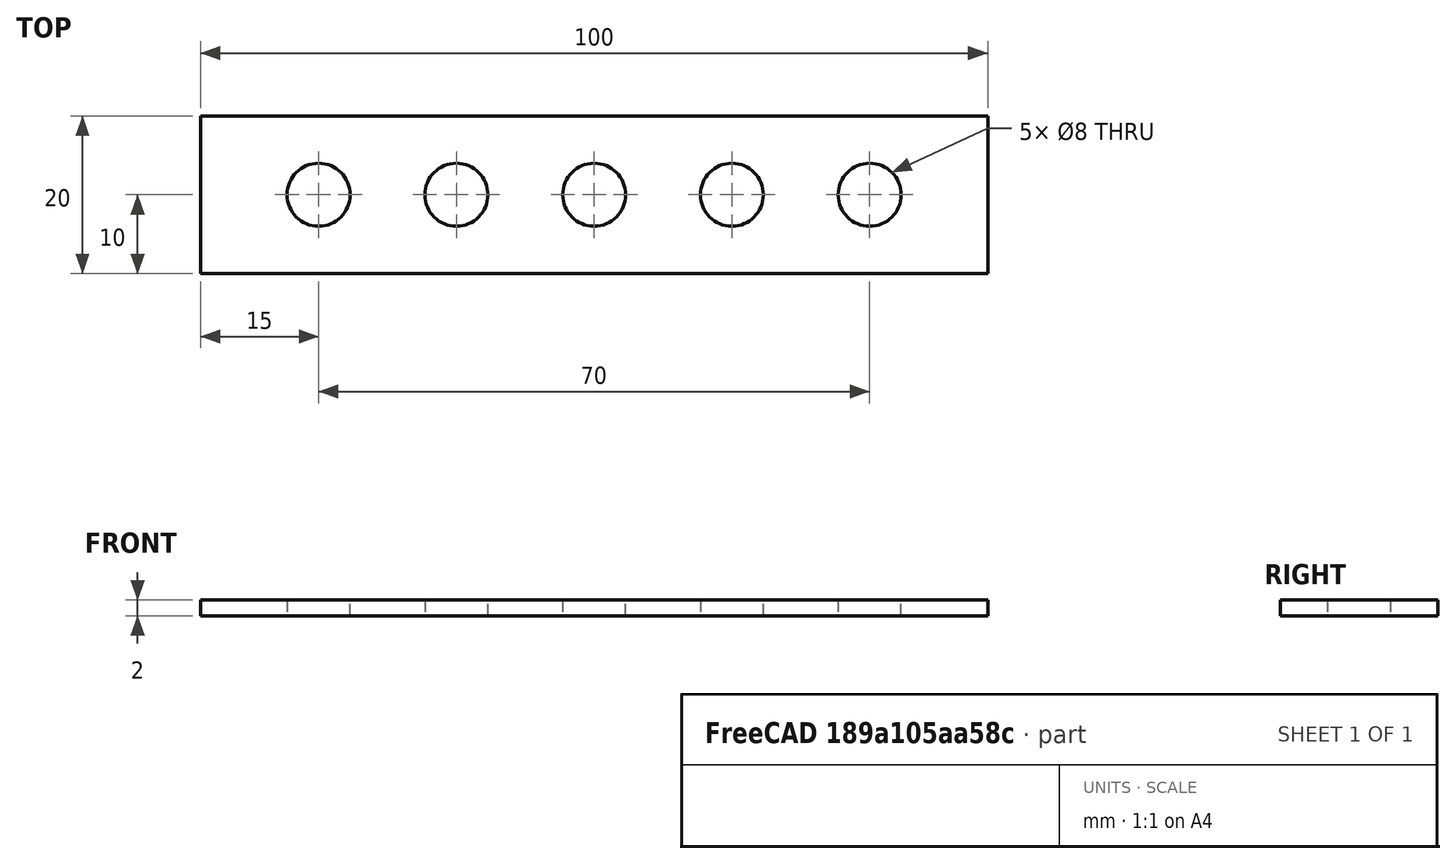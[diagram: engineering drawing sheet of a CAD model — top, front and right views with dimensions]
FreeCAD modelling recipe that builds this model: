
FCSTD DOCUMENT  (FreeCAD 0.20R29410 (Git))
Label: Potentiometer-Base
License: All rights reserved
LicenseURL: https://en.wikipedia.org/wiki/All_rights_reserved
objects: PartDesign::CoordinateSystem×8, App::Link×7, App::DocumentObjectGroup×3, App::FeaturePython×1, Sketcher::SketchObject×1, PartDesign::Pad×1, App::Part×1
note: 11 computed .brp shape members not serialized (recipe doc carries the construction recipe); baked Part::Feature solids carry a one-line shape summary decoded from their .brp
EXTERNAL_REF file=Potentiometer-Support.FCStd obj=LCS_Origin
EXTERNAL_REF file=Potentiometer-Support.FCStd obj=Assembly
EXTERNAL_REF file=Nut-Holder.FCStd obj=LCS_Origin
EXTERNAL_REF file=Nut-Holder.FCStd obj=Assembly

FEATURE [App::DocumentObjectGroup] Parts
FEATURE [PartDesign::CoordinateSystem] LCS_Origin
  AttacherType = Attacher::AttachEngine3D
  MapMode = 2
  Support = -> [X_Axis]
FEATURE [App::DocumentObjectGroup] Constraints
FEATURE [App::FeaturePython] Variables  # WARN: FeaturePython — macro-defined, semantics opaque (R4)
  Type = App::PropertyContainer
FEATURE [App::DocumentObjectGroup] Configurations
FEATURE [Sketcher::SketchObject] Sketch
  FullyConstrained = true
  MapMode = 5
  sketch-geometry (13):
    g0: LineSegment StartX=-50 StartY=10 StartZ=0 EndX=50 EndY=10 EndZ=0
    g1: LineSegment StartX=50 StartY=10 StartZ=0 EndX=50 EndY=-10 EndZ=0
    g2: LineSegment StartX=50 StartY=-10 StartZ=0 EndX=-50 EndY=-10 EndZ=0
    g3: LineSegment StartX=-50 StartY=-10 StartZ=0 EndX=-50 EndY=10 EndZ=0
    g4: LineSegment StartX=-35 StartY=0 StartZ=0 EndX=-17.5 EndY=0 EndZ=0
    g5: LineSegment StartX=-17.5 StartY=0 StartZ=0 EndX=0 EndY=0 EndZ=0
    g6: LineSegment StartX=0 StartY=0 StartZ=0 EndX=17.5 EndY=0 EndZ=0
    g7: LineSegment StartX=17.5 StartY=0 StartZ=0 EndX=35 EndY=0 EndZ=0
    g8: Circle CenterX=-35 CenterY=0 CenterZ=0 NormalX=0 NormalY=0 NormalZ=1 AngleXU=0 Radius=4
    g9: Circle CenterX=-17.5 CenterY=0 CenterZ=0 NormalX=0 NormalY=0 NormalZ=1 AngleXU=0 Radius=4
    g10: Circle CenterX=0 CenterY=0 CenterZ=0 NormalX=0 NormalY=0 NormalZ=1 AngleXU=0 Radius=4
    g11: Circle CenterX=17.5 CenterY=0 CenterZ=0 NormalX=0 NormalY=0 NormalZ=1 AngleXU=0 Radius=4
    g12: Circle CenterX=35 CenterY=0 CenterZ=0 NormalX=0 NormalY=0 NormalZ=1 AngleXU=0 Radius=4
  constraints (33):
    c: Coincident(g0,g1)
    c: Coincident(g1,g2)
    c: Coincident(g2,g3)
    c: Coincident(g3,g0)
    c: Horizontal(g0)
    c: Horizontal(g2)
    c: Vertical(g1)
    c: Vertical(g3)
    c: Symmetric(g1,g0,g-1)
    c: DistanceX(g0,g0) = 100
    c: DistanceY(g1,g1) = 20
    c: Horizontal(g4)
    c: Coincident(g5,g4)
    c: Horizontal(g5)
    c: Coincident(g6,g5)
    c: Horizontal(g6)
    c: Horizontal(g7)
    c: Equal(g6,g5)
    c: Equal(g5,g4)
    c: Symmetric(g4,g7,g-1)
    c: DistanceX(g7,g7) = 17.5
    c: Coincident(g8,g4)
    c: Coincident(g9,g4)
    c: Coincident(g10,g5)
    c: Coincident(g12,g7)
    c: Equal(g12,g11)
    c: Equal(g10,g9)
    c: Equal(g9,g8)
    c: Diameter(g12) = 8
    c: Coincident(g11,g6)
    c: Coincident(g7,g11)
    c: Equal(g10,g11)
    c: Equal(g6,g7)
FEATURE [PartDesign::Pad] Pad  label="Base Plate"
  Direction = (0,0,1)
  Length = 2
  Length2 = 10
  Profile = -> Sketch
  ReferenceAxis = -> Sketch [N_Axis]
  Refine = true
  Type = 0
FEATURE [PartDesign::CoordinateSystem] LCS_Pot_1
  AttacherType = Attacher::AttachEngine3D
  MapMode = 45
  Placement = pos=(-35,1e-16,2) rot=(0,0,-1;0rad)
  Support = -> [Pad]
FEATURE [PartDesign::CoordinateSystem] LCS_Pot_2
  AttacherType = Attacher::AttachEngine3D
  MapMode = 45
  Placement = pos=(-17.5,1e-16,2) rot=(0,0,1;0rad)
  Support = -> [Pad]
FEATURE [PartDesign::CoordinateSystem] LCS_Pot_3
  AttacherType = Attacher::AttachEngine3D
  MapMode = 45
  Placement = pos=(1.89e-14,1e-16,2) rot=(0,0,1;0rad)
  Support = -> [Pad]
FEATURE [PartDesign::CoordinateSystem] LCS_Pot_4
  AttacherType = Attacher::AttachEngine3D
  MapMode = 45
  Placement = pos=(17.5,1e-16,2) rot=(0,0,1;0rad)
  Support = -> [Pad]
FEATURE [PartDesign::CoordinateSystem] LCS_Pot_5
  AttacherType = Attacher::AttachEngine3D
  MapMode = 45
  Placement = pos=(35,1e-16,2) rot=(0,0,1;0rad)
  Support = -> [Pad]
FEATURE [PartDesign::CoordinateSystem] LCS_Left_Holder
  AttacherType = Attacher::AttachEngine3D
  AttachmentOffset = pos=(-10,0,0) rot=(0,0,1;0rad)
  MapMode = 2
  Placement = pos=(-45,3.74728e-07,2) rot=(0,0,-1;0rad)
  Support = -> [LCS_Pot_1]
FEATURE [PartDesign::CoordinateSystem] LCS_Right_Holder
  AttacherType = Attacher::AttachEngine3D
  AttachmentOffset = pos=(10,0,0) rot=(0,0,1;0rad)
  MapMode = 2
  Placement = pos=(45,1.63695e-06,2) rot=(0,0,1;0rad)
  Support = -> [LCS_Pot_5]
FEATURE [App::Link] Pot_1
  AttachedBy = #LCS_Origin
  AttachedTo = Parent Assembly#LCS_Pot_1
  LinkPlacement = pos=(-35,1e-16,2) rot=(0,0,-1;0rad)
  LinkedObject = -> <external Potentiometer-Support.FCStd>#Assembly
  Placement = pos=(-35,1e-16,2) rot=(0,0,-1;0rad)
  SolverId = Asm4EE
  expr: Placement = LCS_Pot_1.Placement * AttachmentOffset * Potentiometer_Support#LCS_Origin.Placement ^ -1
FEATURE [App::Link] Pot_2
  AttachedBy = #LCS_Origin
  AttachedTo = Parent Assembly#LCS_Pot_2
  LinkPlacement = pos=(-17.5,1e-16,2) rot=(0,0,1;0rad)
  LinkedObject = -> <external Potentiometer-Support.FCStd>#Assembly
  Placement = pos=(-17.5,1e-16,2) rot=(0,0,1;0rad)
  SolverId = Asm4EE
  expr: Placement = LCS_Pot_2.Placement * AttachmentOffset * Potentiometer_Support#LCS_Origin.Placement ^ -1
FEATURE [App::Link] Pot_3
  AttachedBy = #LCS_Origin
  AttachedTo = Parent Assembly#LCS_Pot_3
  LinkPlacement = pos=(1.89e-14,1e-16,2) rot=(0,0,1;0rad)
  LinkedObject = -> <external Potentiometer-Support.FCStd>#Assembly
  Placement = pos=(1.89e-14,1e-16,2) rot=(0,0,1;0rad)
  SolverId = Asm4EE
  expr: Placement = LCS_Pot_3.Placement * AttachmentOffset * Potentiometer_Support#LCS_Origin.Placement ^ -1
FEATURE [App::Link] Pot_4
  AttachedBy = #LCS_Origin
  AttachedTo = Parent Assembly#LCS_Pot_4
  LinkPlacement = pos=(17.5,1e-16,2) rot=(0,0,1;0rad)
  LinkedObject = -> <external Potentiometer-Support.FCStd>#Assembly
  Placement = pos=(17.5,1e-16,2) rot=(0,0,1;0rad)
  SolverId = Asm4EE
  expr: Placement = LCS_Pot_4.Placement * AttachmentOffset * Potentiometer_Support#LCS_Origin.Placement ^ -1
FEATURE [App::Link] Pot_5
  AttachedBy = #LCS_Origin
  AttachedTo = Parent Assembly#LCS_Pot_5
  LinkPlacement = pos=(35,1e-16,2) rot=(0,0,1;0rad)
  LinkedObject = -> <external Potentiometer-Support.FCStd>#Assembly
  Placement = pos=(35,1e-16,2) rot=(0,0,1;0rad)
  SolverId = Asm4EE
  expr: Placement = LCS_Pot_5.Placement * AttachmentOffset * Potentiometer_Support#LCS_Origin.Placement ^ -1
FEATURE [App::Link] Left_Nut_Holder
  AttachedBy = #LCS_Origin
  AttachedTo = Parent Assembly#LCS_Left_Holder
  LinkPlacement = pos=(-45,3.74728e-07,2) rot=(0,0,-1;0rad)
  LinkedObject = -> <external Nut-Holder.FCStd>#Assembly
  Placement = pos=(-45,3.74728e-07,2) rot=(0,0,-1;0rad)
  SolverId = Asm4EE
  expr: Placement = LCS_Left_Holder.Placement * AttachmentOffset * Nut_Holder#LCS_Origin.Placement ^ -1
FEATURE [App::Link] Right_Nut_Holder
  AttachedBy = #LCS_Origin
  AttachedTo = Parent Assembly#LCS_Right_Holder
  LinkPlacement = pos=(45,1.63695e-06,2) rot=(0,0,1;0rad)
  LinkedObject = -> <external Nut-Holder.FCStd>#Assembly
  Placement = pos=(45,1.63695e-06,2) rot=(0,0,1;0rad)
  SolverId = Asm4EE
  expr: Placement = LCS_Right_Holder.Placement * AttachmentOffset * Nut_Holder#LCS_Origin.Placement ^ -1
FEATURE [App::Part] Assembly
  AssemblyType = Part::Link
  Group = -> [LCS_Origin,Constraints,Variables,Configurations,Sketch,Pad,LCS_Pot_1,LCS_Pot_2,LCS_Pot_3,LCS_Pot_4,LCS_Pot_5,LCS_Left_Holder,LCS_Right_Holder,Left_Nut_Holder,Right_Nut_Holder,Pot_1,Pot_2,Pot_3,Pot_4,Pot_5]
  Origin = -> Origin
  Type = Assembly

RESOLVED EXTERNAL PARTS (link-assembly join: the EXTERNAL_REF files above that resolve inside this repo's crawl, each included once):
---- part Nut-Holder.FCStd = doc fcstd_a03749667bbf ----
FCSTD DOCUMENT  (FreeCAD 0.20R29410 (Git))
Label: Nut-Holder
License: All rights reserved
LicenseURL: https://en.wikipedia.org/wiki/All_rights_reserved
objects: App::DocumentObjectGroup×3, PartDesign::CoordinateSystem×3, Sketcher::SketchObject×2, App::FeaturePython×1, PartDesign::Pad×1, PartDesign::Pocket×1, PartDesign::Body×1, App::Part×1
note: 10 computed .brp shape members not serialized (recipe doc carries the construction recipe); baked Part::Feature solids carry a one-line shape summary decoded from their .brp

FEATURE [App::DocumentObjectGroup] Parts
FEATURE [PartDesign::CoordinateSystem] LCS_Origin
  AttacherType = Attacher::AttachEngine3D
  MapMode = 2
  Support = -> [X_Axis]
FEATURE [App::DocumentObjectGroup] Constraints
FEATURE [App::FeaturePython] Variables  # WARN: FeaturePython — macro-defined, semantics opaque (R4)
  Type = App::PropertyContainer
  diameter = 8.6
  height = 9.2
  nut_width = 6
  pocket_height = 4
  expr: diameter = nut_width + 1 + 2 * 0.8
FEATURE [App::DocumentObjectGroup] Configurations
FEATURE [Sketcher::SketchObject] Sketch
  FullyConstrained = true
  MapMode = 5
  expr: Constraints[1] = Variables.diameter
  sketch-geometry (1):
    g0: Circle CenterX=0 CenterY=0 CenterZ=0 NormalX=0 NormalY=0 NormalZ=1 AngleXU=0 Radius=4.3
  constraints (2):
    c: Coincident(g0,g-1)
    c: Diameter(g0) = 8.6
FEATURE [PartDesign::Pad] Pad  label="Enclosure"
  Direction = (0,0,1)
  Length = 9.2
  Length2 = 10
  Profile = -> Sketch
  ReferenceAxis = -> Sketch [N_Axis]
  Refine = true
  Type = 0
  expr: Length = Variables.height
FEATURE [PartDesign::CoordinateSystem] LCS_Origin001
  AttacherType = Attacher::AttachEngine3D
  MapMode = 2
  Support = -> [X_Axis001]
FEATURE [Sketcher::SketchObject] Sketch003
  AttachmentOffset = pos=(0,0,9.2) rot=(0,0,1;0rad)
  FullyConstrained = true
  MapMode = 5
  Placement = pos=(0,0,9.2) rot=(0,0,1;0rad)
  Support = -> [XY_Plane001]
  expr: .AttachmentOffset.Base.z = Variables.height
  expr: Constraints[19] = Variables.nut_width + 1
  sketch-geometry (7):
    g0: LineSegment StartX=-3.5 StartY=0 StartZ=0 EndX=-1.75 EndY=-3.03109 EndZ=0
    g1: LineSegment StartX=-1.75 StartY=-3.03109 StartZ=0 EndX=1.75 EndY=-3.03109 EndZ=0
    g2: LineSegment StartX=1.75 StartY=-3.03109 StartZ=0 EndX=3.5 EndY=0 EndZ=0
    g3: LineSegment StartX=3.5 StartY=0 StartZ=0 EndX=1.75 EndY=3.03109 EndZ=0
    g4: LineSegment StartX=1.75 StartY=3.03109 StartZ=0 EndX=-1.75 EndY=3.03109 EndZ=0
    g5: LineSegment StartX=-1.75 StartY=3.03109 StartZ=0 EndX=-3.5 EndY=0 EndZ=0
    g6: Circle CenterX=0 CenterY=0 CenterZ=0 NormalX=0 NormalY=0 NormalZ=1 AngleXU=0 Radius=3.5
  constraints (16):
    c: Coincident(g0,g1)
    c: Coincident(g1,g2)
    c: Coincident(g2,g3)
    c: Coincident(g3,g4)
    c: Coincident(g4,g5)
    c: Coincident(g5,g0)
    c: Equal(g0, g1-g5) x5
    c: PointOnObject(g0,g6)
    c: PointOnObject(g1,g6)
    c: PointOnObject(g2,g6)
    c: PointOnObject(g3,g6)
    c: PointOnObject(g4,g6)
    c: PointOnObject(g5,g6)
    c: Coincident(g6,g-1)
    c: PointOnObject(g5,g-1)
    c: DistanceX(g0,g2) = 7
FEATURE [PartDesign::Pocket] Pocket  label="Nut Pocket"
  BaseFeature = -> Pad
  Direction = (0,0,-1)
  Length = 4
  Length2 = 5
  Profile = -> Sketch003
  ReferenceAxis = -> Sketch003 [N_Axis]
  Refine = true
  Type = 0
  expr: Length = Variables.pocket_height
FEATURE [PartDesign::Body] Body
  Group = -> [LCS_Origin001,Pad,Sketch,Sketch003,Pocket]
  Origin = -> Origin001
  Tip = -> Pocket
FEATURE [PartDesign::CoordinateSystem] LCS_Top
  AttacherType = Attacher::AttachEngine3D
  MapMode = 45
  Placement = pos=(-1e-16,3e-16,9.2) rot=(0,0,1;0rad)
  Support = -> [Pocket]
FEATURE [App::Part] Assembly
  AssemblyType = Part::Link
  Group = -> [LCS_Origin,Constraints,Variables,Configurations,Body,LCS_Top]
  Origin = -> Origin
  Type = Assembly
---- part Potentiometer-Support.FCStd = doc fcstd_ed71becc3c36 ----
FCSTD DOCUMENT  (FreeCAD 0.20R29410 (Git))
Label: Potentiometer-Support
License: All rights reserved
LicenseURL: https://en.wikipedia.org/wiki/All_rights_reserved
objects: App::DocumentObjectGroup×3, Sketcher::SketchObject×3, PartDesign::CoordinateSystem×2, PartDesign::Pad×2, App::FeaturePython×1, PartDesign::Pocket×1, PartDesign::Body×1, App::Part×1
note: 12 computed .brp shape members not serialized (recipe doc carries the construction recipe); baked Part::Feature solids carry a one-line shape summary decoded from their .brp

FEATURE [App::DocumentObjectGroup] Parts
FEATURE [PartDesign::CoordinateSystem] LCS_Origin
  AttacherType = Attacher::AttachEngine3D
  MapMode = 2
  Support = -> [X_Axis]
FEATURE [App::DocumentObjectGroup] Constraints
FEATURE [App::FeaturePython] Variables  # WARN: FeaturePython — macro-defined, semantics opaque (R4)
  Type = App::PropertyContainer
FEATURE [App::DocumentObjectGroup] Configurations
FEATURE [PartDesign::CoordinateSystem] LCS_Origin001
  AttacherType = Attacher::AttachEngine3D
  MapMode = 2
  Support = -> [X_Axis001]
FEATURE [Sketcher::SketchObject] Sketch
  FullyConstrained = true
  MapMode = 5
  Support = -> [XY_Plane001]
  sketch-geometry (4):
    g0: LineSegment StartX=-6.05 StartY=7.05 StartZ=0 EndX=6.05 EndY=7.05 EndZ=0
    g1: LineSegment StartX=6.05 StartY=7.05 StartZ=0 EndX=6.05 EndY=-7.05 EndZ=0
    g2: LineSegment StartX=6.05 StartY=-7.05 StartZ=0 EndX=-6.05 EndY=-7.05 EndZ=0
    g3: LineSegment StartX=-6.05 StartY=-7.05 StartZ=0 EndX=-6.05 EndY=7.05 EndZ=0
  constraints (11):
    c: Coincident(g0,g1)
    c: Coincident(g1,g2)
    c: Coincident(g2,g3)
    c: Coincident(g3,g0)
    c: Horizontal(g0)
    c: Horizontal(g2)
    c: Vertical(g1)
    c: Vertical(g3)
    c: Symmetric(g0,g1,g-1)
    c: DistanceY(g1,g1) = 14.1
    c: DistanceX(g0,g0) = 12.1
FEATURE [PartDesign::Pad] Pad  label="Base"
  Direction = (0,0,1)
  Length = 3
  Length2 = 10
  Profile = -> Sketch
  ReferenceAxis = -> Sketch [N_Axis]
  Refine = true
  Type = 0
FEATURE [Sketcher::SketchObject] Sketch001
  ExternalGeometry = -> [Pad]
  FullyConstrained = true
  MapMode = 5
  Placement = pos=(0,0,3) rot=(0,0,1;0rad)
  Support = -> [Pad]
  sketch-geometry (8):
    g0: LineSegment StartX=-6.05 StartY=7.05 StartZ=0 EndX=6.05 EndY=7.05 EndZ=0
    g1: LineSegment StartX=6.05 StartY=7.05 StartZ=0 EndX=6.05 EndY=-7.05 EndZ=0
    g2: LineSegment StartX=6.05 StartY=-7.05 StartZ=0 EndX=-6.05 EndY=-7.05 EndZ=0
    g3: LineSegment StartX=-6.05 StartY=-7.05 StartZ=0 EndX=-6.05 EndY=7.05 EndZ=0
    g4: LineSegment StartX=-5.25 StartY=6.25 StartZ=0 EndX=5.25 EndY=6.25 EndZ=0
    g5: LineSegment StartX=5.25 StartY=6.25 StartZ=0 EndX=5.25 EndY=-6.25 EndZ=0
    g6: LineSegment StartX=5.25 StartY=-6.25 StartZ=0 EndX=-5.25 EndY=-6.25 EndZ=0
    g7: LineSegment StartX=-5.25 StartY=-6.25 StartZ=0 EndX=-5.25 EndY=6.25 EndZ=0
  constraints (21):
    c: Coincident(g0,g1)
    c: Coincident(g1,g2)
    c: Coincident(g2,g3)
    c: Coincident(g3,g0)
    c: Horizontal(g0)
    c: Horizontal(g2)
    c: Vertical(g1)
    c: Vertical(g3)
    c: Coincident(g0,g-3)
    c: Coincident(g1,g-4)
    c: Coincident(g4,g5)
    c: Coincident(g5,g6)
    c: Coincident(g6,g7)
    c: Coincident(g7,g4)
    c: Horizontal(g4)
    c: Horizontal(g6)
    c: Vertical(g5)
    c: Vertical(g7)
    c: Symmetric(g5,g4,g-1)
    c: DistanceX(g0,g4) = 0.8
    c: DistanceY(g4,g0) = 0.8
FEATURE [PartDesign::Pad] Pad001  label="Walls"
  BaseFeature = -> Pad
  Direction = (0,0,1)
  Length = 4
  Length2 = 10
  Profile = -> Sketch001
  ReferenceAxis = -> Sketch001 [N_Axis]
  Refine = true
  Type = 0
FEATURE [Sketcher::SketchObject] Sketch002
  FullyConstrained = true
  MapMode = 5
  Placement = pos=(0,0,3) rot=(0,0,1;0rad)
  Support = -> [Pad001]
  sketch-geometry (1):
    g0: Circle CenterX=0 CenterY=0 CenterZ=0 NormalX=0 NormalY=0 NormalZ=1 AngleXU=0 Radius=4
  constraints (2):
    c: Coincident(g0,g-1)
    c: Diameter(g0) = 8
FEATURE [PartDesign::Pocket] Pocket
  BaseFeature = -> Pad001
  Direction = (0,0,-1)
  Length = 5
  Length2 = 5
  Profile = -> Sketch002
  ReferenceAxis = -> Sketch002 [N_Axis]
  Refine = true
  Type = 0
FEATURE [PartDesign::Body] Body
  Group = -> [LCS_Origin001,Sketch,Pad,Sketch001,Pad001,Sketch002,Pocket]
  Origin = -> Origin001
  Tip = -> Pocket
FEATURE [App::Part] Assembly
  AssemblyType = Part::Link
  Group = -> [LCS_Origin,Constraints,Variables,Configurations,Body]
  Origin = -> Origin
  Type = Assembly
